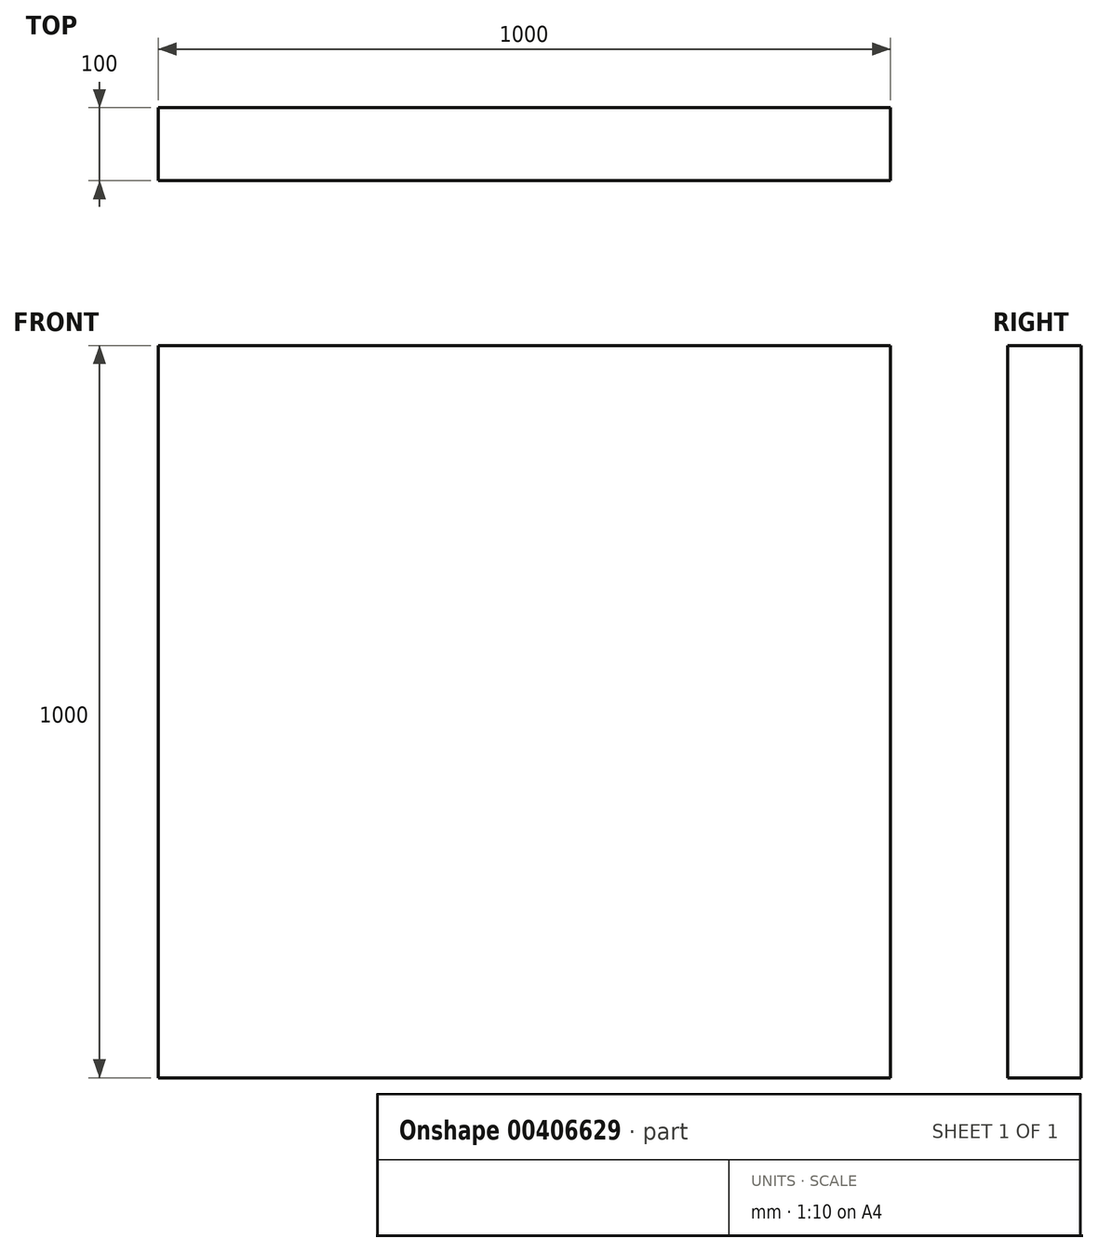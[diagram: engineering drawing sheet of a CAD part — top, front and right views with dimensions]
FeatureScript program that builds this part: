
annotation { "Feature Type Name" : "Feature", "Feature Type Description" : "" }
export const myFeature = defineFeature(function(context is Context, id is Id, definition is map)
    precondition{}
    {
        {
            var Q0;
            Q0=qCreatedBy(makeId("Front.planeOp"),FACE);
            var sketch = newSketch(context, id + "F0", { "sketchPlane" : qUnion([Q0])});
            skLineSegment(sketch, "E0.bottom", {"start": v(-500, 500) * mm, "end": v(500, 500) * mm});
            skLineSegment(sketch, "E0.top", {"start": v(-500, -500) * mm, "end": v(500, -500) * mm});
            skLineSegment(sketch, "E0.left", {"start": v(-500, 500) * mm, "end": v(-500, -500) * mm});
            skLineSegment(sketch, "E0.right", {"start": v(500, 500) * mm, "end": v(500, -500) * mm});
            skPoint(sketch, "E0.middle", {"position": v(0, 0) * mm});
            skSolve(sketch);
        }
        {
            var Q0;
            Q0 = qSketchRegion(id + "F0", true);
            extrude(context, id + "F1", {"entities" : qUnion([Q0]), "endBound" : BoundingType.SYMMETRIC, "depth" : 1000 * mm});
        }
        {
            var Q0;
            Q0=makeQuery(id+"F1.opExtrude","CAP_FACE",FACE,{"disambiguationData":[OSD([sQuery(id+"F0.wireOp",EDGE,"E0.bottom"),sQuery(id+"F0.wireOp",EDGE,"E0.top"),sQuery(id+"F0.wireOp",EDGE,"E0.left"),sQuery(id+"F0.wireOp",EDGE,"E0.right")])],"isStart":false});
            cPlane(context, id + "F2", {"entities" : qUnion([Q0]), "cplaneType" : CPlaneType.OFFSET, "offset" : 100 * mm, "oppositeDirection" : true, "width" : 152.4 * mm, "height" : 152.4 * mm});
        }
        {
            var Q0;
            Q0=qCreatedBy(id+"F2.planeOp",FACE);
            var sketch = newSketch(context, id + "F3", { "sketchPlane" : qUnion([Q0])});
            skLineSegment(sketch, "E1.0", {"start": v(500, 500) * mm, "end": v(500, -500) * mm});
            skLineSegment(sketch, "E2.0", {"start": v(-500, 500) * mm, "end": v(500, 500) * mm});
            skLineSegment(sketch, "E3.0", {"start": v(-500, 500) * mm, "end": v(-500, -500) * mm});
            skPoint(sketch, "E4.0", {"position": v(-500, 500) * mm});
            skLineSegment(sketch, "E5.0", {"start": v(-500, -500) * mm, "end": v(500, -500) * mm});
            skSolve(sketch);
        }
        {
            var Q0;
            Q0 = qSketchRegion(id + "F3", true);
            extrude(context, id + "F4", {"entities" : qUnion([Q0]), "operationType" : NewBodyOperationType.REMOVE, "oppositeDirection" : true, "depth" : 1000 * mm});
        }
    });
